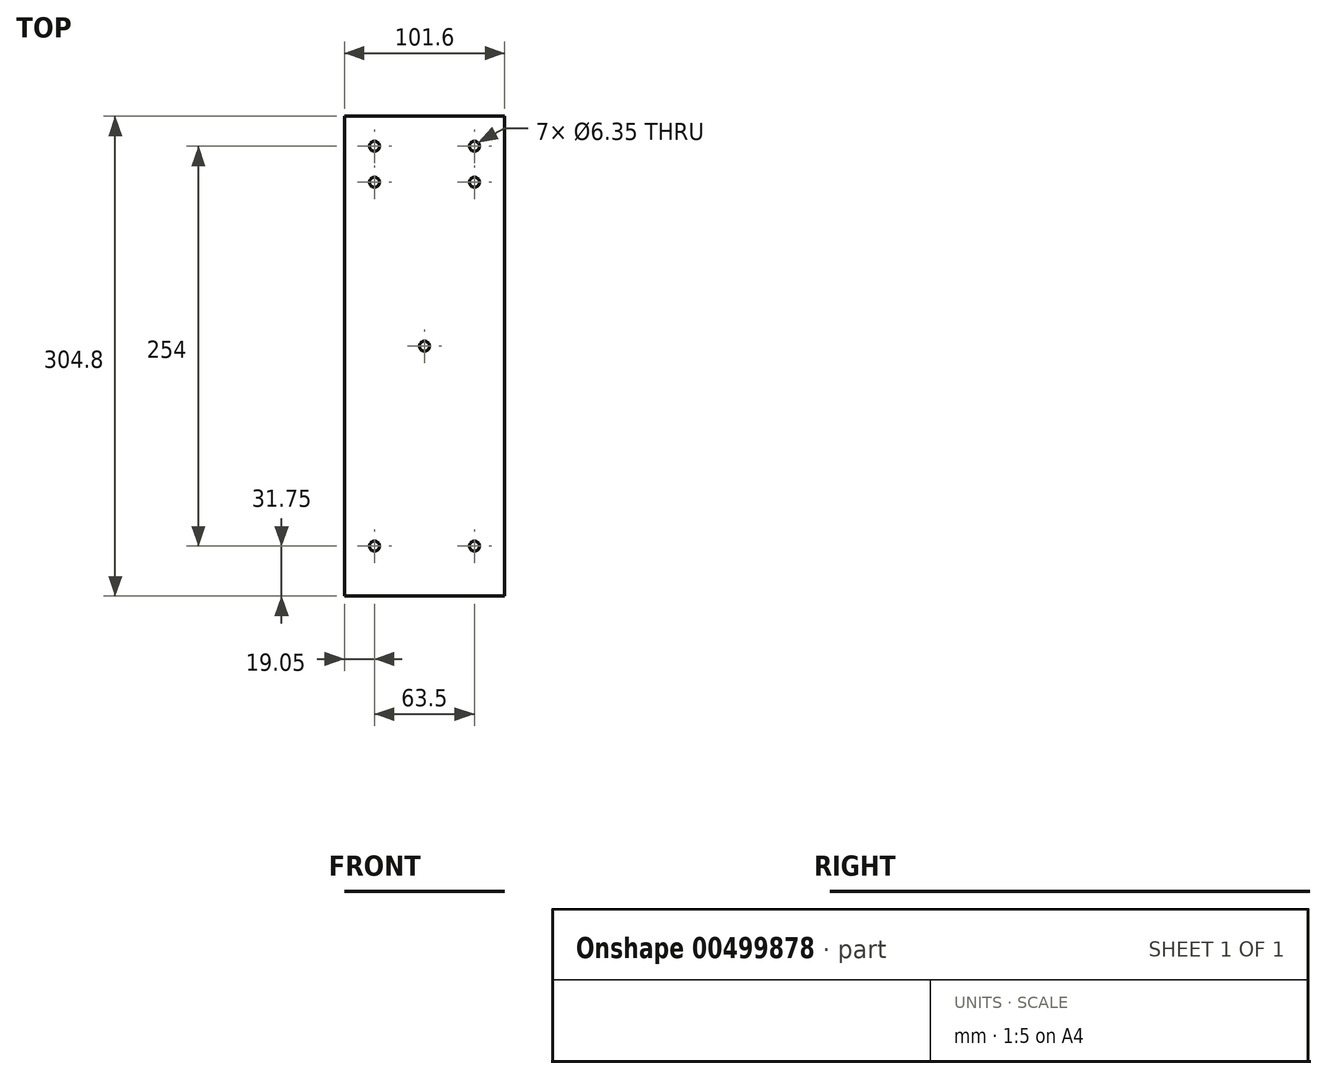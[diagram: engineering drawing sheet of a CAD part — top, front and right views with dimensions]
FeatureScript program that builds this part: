
annotation { "Feature Type Name" : "Feature", "Feature Type Description" : "" }
export const myFeature = defineFeature(function(context is Context, id is Id, definition is map)
    precondition{}
    {
        {
            var Q0;
            Q0=qCreatedBy(makeId("Top.planeOp"),FACE);
            var sketch = newSketch(context, id + "F0", { "sketchPlane" : qUnion([Q0])});
            skLineSegment(sketch, "E0.bottom", {"start": v(50.8, -152.4) * mm, "end": v(-50.8, -152.4) * mm});
            skLineSegment(sketch, "E0.top", {"start": v(50.8, 152.4) * mm, "end": v(-50.8, 152.4) * mm, "construction": true});
            skLineSegment(sketch, "E0.left", {"start": v(50.8, -152.4) * mm, "end": v(50.8, 152.4) * mm});
            skLineSegment(sketch, "E0.right", {"start": v(-50.8, -152.4) * mm, "end": v(-50.8, 152.4) * mm});
            skPoint(sketch, "E0.middle", {"position": v(0, 0) * mm});
            skLineSegment(sketch, "E1", {"start": v(0, 152.4) * mm, "end": v(0, -152.4) * mm, "construction": true});
            skLineSegment(sketch, "E2", {"start": v(-50.8, 152.4) * mm, "end": v(50.8, 152.4) * mm});
            skSolve(sketch);
        }
        {
            var Q0;
            Q0 = qSketchRegion(id + "F0", true);
            extrude(context, id + "F1", {"entities" : qUnion([Q0]), "depth" : 1 / 203.2 * mm});
        }
        {
            var Q0;
            Q0=makeQuery(id+"F1.opExtrude","CAP_FACE",FACE,{"disambiguationData":[OSD([sQuery(id+"F0.wireOp",EDGE,"E0.bottom"),sQuery(id+"F0.wireOp",EDGE,"E0.top"),sQuery(id+"F0.wireOp",EDGE,"E0.left"),sQuery(id+"F0.wireOp",EDGE,"E0.right")])],"isStart":false});
            var sketch = newSketch(context, id + "F2", { "sketchPlane" : qUnion([Q0])});
            skLineSegment(sketch, "E3", {"start": v(-50.8, -120.65) * mm, "end": v(50.8, -120.65) * mm, "construction": true});
            skLineSegment(sketch, "E4.bottom", {"start": v(31.75, -120.65) * mm, "end": v(-31.75, -120.65) * mm});
            skLineSegment(sketch, "E4.top", {"start": v(31.75, 133.35) * mm, "end": v(-31.75, 133.35) * mm});
            skLineSegment(sketch, "E4.left", {"start": v(31.75, -120.65) * mm, "end": v(31.75, 133.35) * mm, "construction": true});
            skLineSegment(sketch, "E4.right", {"start": v(-31.75, -120.65) * mm, "end": v(-31.75, 133.35) * mm, "construction": true});
            skPoint(sketch, "E4.middle", {"position": v(0, 6.35) * mm});
            skPoint(sketch, "E5", {"position": v(-31.75, 110.49) * mm});
            skPoint(sketch, "E6", {"position": v(31.75, 110.49) * mm});
            skLineSegment(sketch, "E7", {"start": v(-31.75, 110.49) * mm, "end": v(31.75, 110.49) * mm, "construction": true});
            skLineSegment(sketch, "E8", {"start": v(0, -120.65) * mm, "end": v(0, 133.35) * mm, "construction": true});
            skSolve(sketch);
        }
        {
            var Q0;
            Q0=sQuery(id+"F2.wireOp",VERTEX,"E4.right.end");
            var Q1;
            Q1=sQuery(id+"F2.wireOp",VERTEX,"E4.top.start");
            var Q2;
            Q2=sQuery(id+"F2.wireOp",VERTEX,"E4.bottom.start");
            var Q3;
            Q3=sQuery(id+"F2.wireOp",VERTEX,"E4.bottom.end");
            var Q4;
            Q4=sQuery(id+"F2.wireOp",VERTEX,"E4.middle");
            var Q5;
            Q5=sQuery(id+"F2.wireOp",VERTEX,"E5");
            var Q6;
            Q6=sQuery(id+"F2.wireOp",VERTEX,"E6");
            var Q7;
            Q7=makeQuery(id+"F1.opExtrude","SWEPT_BODY",BODY,{"disambiguationData":[OSD([sQuery(id+"F0.wireOp",EDGE,"E0.bottom"),sQuery(id+"F0.wireOp",EDGE,"E0.top"),sQuery(id+"F0.wireOp",EDGE,"E0.left"),sQuery(id+"F0.wireOp",EDGE,"E0.right")])]});
            hole(context, id + "F3", {"style" : HoleStyle.SIMPLE, "endStyle" : HoleEndStyle.THROUGH, "holeDiameter" : 6.35 * mm, "isTappedThrough" : true, "tappedDepth" : 12.7 * mm, "tapClearance" : 3, "locations" : qUnion([Q0, Q1, Q2, Q3, Q4, Q5, Q6]), "scope" : qUnion([Q7])});
        }
    });
